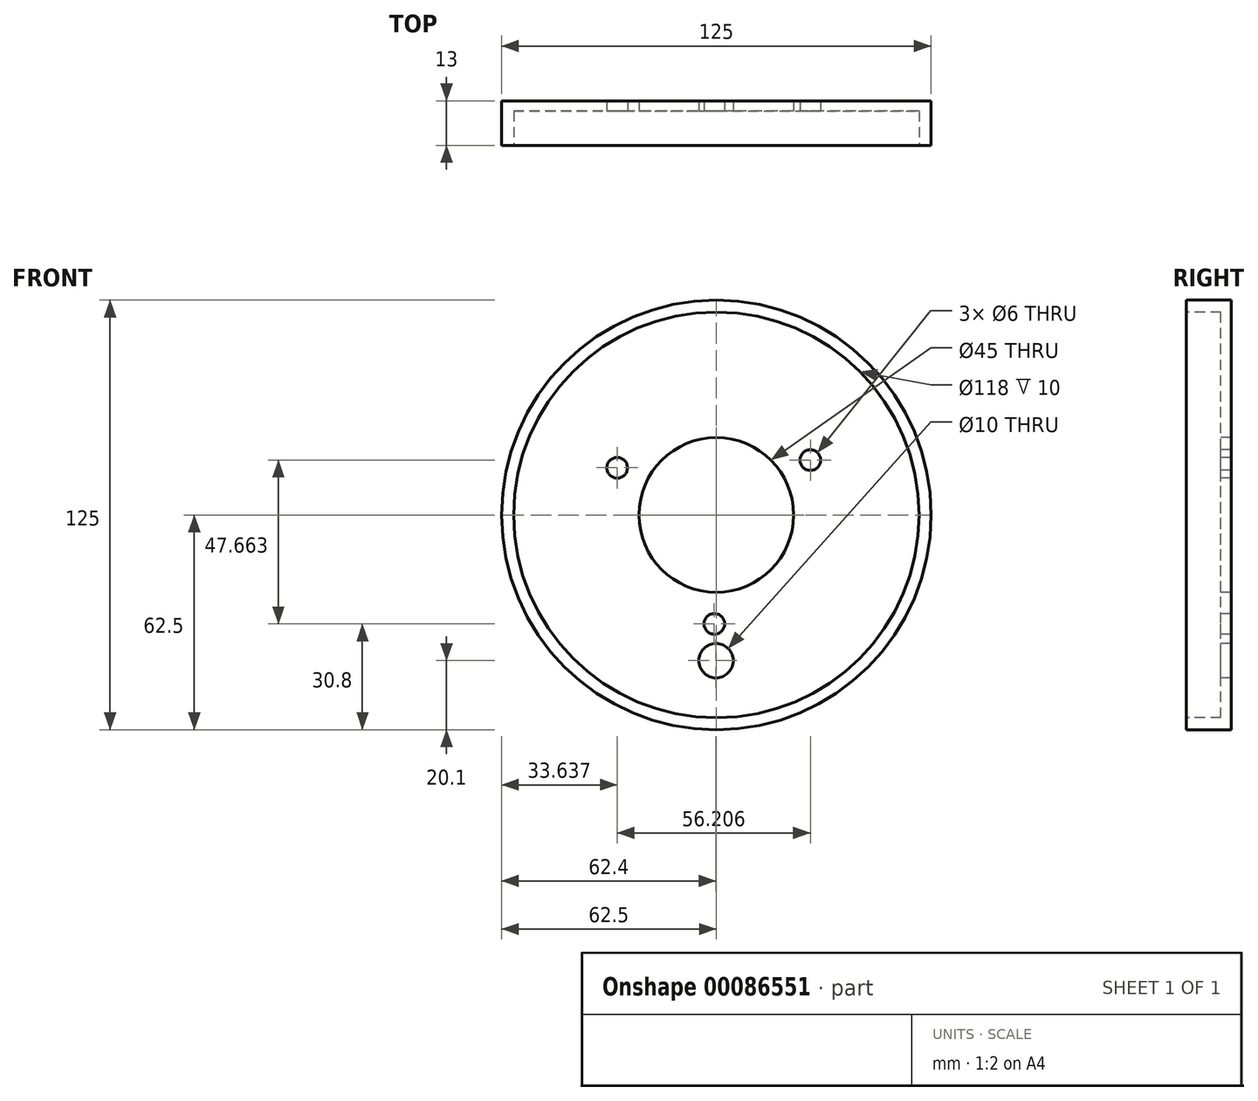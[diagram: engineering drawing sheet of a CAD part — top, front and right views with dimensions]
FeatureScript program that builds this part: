
annotation { "Feature Type Name" : "Feature", "Feature Type Description" : "" }
export const myFeature = defineFeature(function(context is Context, id is Id, definition is map)
    precondition{}
    {
        {
            var Q0;
            Q0=qCreatedBy(makeId("Front.planeOp"),FACE);
            var sketch = newSketch(context, id + "F0", { "sketchPlane" : qUnion([Q0])});
            skCircle(sketch, "E0", {"center": v(0, 0) * mm, "radius": 62.5 * mm});
            skSolve(sketch);
        }
        {
            var Q0;
            Q0=makeQuery(id+"F0.imprint","IMPRINT",FACE,{"disambiguationData":[TD([[makeQuery(id+"F0.imprint","IMPRINT",EDGE,{"derivedFrom":sQuery(id+"F0.wireOp",EDGE,"E0")}),1.0]])]});
            extrude(context, id + "F1", {"entities" : qUnion([Q0]), "offsetDistance" : 25 * mm, "depth" : 13 * mm});
        }
        {
            var Q0;
            Q0=makeQuery(id+"F1.opExtrude","CAP_FACE",FACE,{"disambiguationData":[OSD([sQuery(id+"F0.wireOp",EDGE,"E0")])],"isStart":false});
            var sketch = newSketch(context, id + "F2", { "sketchPlane" : qUnion([Q0])});
            skLineSegment(sketch, "E1.bottom", {"start": v(146.15, -111.65) * mm, "end": v(-146.15, -111.65) * mm});
            skLineSegment(sketch, "E1.top", {"start": v(146.15, 111.65) * mm, "end": v(-146.15, 111.65) * mm});
            skLineSegment(sketch, "E1.left", {"start": v(146.15, -111.65) * mm, "end": v(146.15, 111.65) * mm});
            skLineSegment(sketch, "E1.right", {"start": v(-146.15, -111.65) * mm, "end": v(-146.15, 111.65) * mm});
            skPoint(sketch, "E2", {"position": v(0, 0) * mm});
            skPoint(sketch, "E3", {"position": v(-28.86, 13.73) * mm});
            skPoint(sketch, "E4", {"position": v(27.34, 15.96) * mm});
            skPoint(sketch, "E5", {"position": v(-0.6, -31.7) * mm});
            skLineSegment(sketch, "E6", {"start": v(-28.86, 13.73) * mm, "end": v(27.34, 15.96) * mm, "construction": true});
            skPoint(sketch, "E7", {"position": v(-0.1, -42.4) * mm});
            skSolve(sketch);
        }
        {
            var Q0;
            Q0=sQuery(id+"F2.wireOp",VERTEX,"E3");
            var Q1;
            Q1=sQuery(id+"F2.wireOp",VERTEX,"E4");
            var Q2;
            Q2=sQuery(id+"F2.wireOp",VERTEX,"E5");
            var Q3;
            Q3=makeQuery(id+"F1.opExtrude","SWEPT_BODY",BODY,{"disambiguationData":[OSD([sQuery(id+"F0.wireOp",EDGE,"E0")])]});
            hole(context, id + "F3", {"style" : HoleStyle.SIMPLE, "endStyle" : HoleEndStyle.THROUGH, "holeDiameter" : 6 * mm, "majorDiameter" : 5 * mm, "locations" : qUnion([Q0, Q1, Q2]), "scope" : qUnion([Q3]), "isTappedThrough" : true, "tappedDepth" : 12 * mm, "tapClearance" : 3});
        }
        {
            var Q0;
            Q0=sQuery(id+"F2.wireOp",VERTEX,"E2");
            var Q1;
            Q1=makeQuery(id+"F1.opExtrude","SWEPT_BODY",BODY,{"disambiguationData":[OSD([sQuery(id+"F0.wireOp",EDGE,"E0")])]});
            hole(context, id + "F4", {"style" : HoleStyle.C_BORE, "endStyle" : HoleEndStyle.THROUGH, "holeDiameter" : 45 * mm, "cBoreDiameter" : 118 * mm, "cBoreDepth" : 10 * mm, "majorDiameter" : 5 * mm, "locations" : qUnion([Q0]), "scope" : qUnion([Q1]), "isTappedThrough" : true, "tappedDepth" : 12 * mm, "tapClearance" : 3});
        }
        {
            var Q0;
            Q0=sQuery(id+"F2.wireOp",VERTEX,"E7");
            var Q1;
            Q1=makeQuery(id+"F1.opExtrude","SWEPT_BODY",BODY,{"disambiguationData":[OSD([sQuery(id+"F0.wireOp",EDGE,"E0")])]});
            hole(context, id + "F5", {"style" : HoleStyle.SIMPLE, "endStyle" : HoleEndStyle.THROUGH, "holeDiameter" : 10 * mm, "majorDiameter" : 5 * mm, "locations" : qUnion([Q0]), "scope" : qUnion([Q1]), "isTappedThrough" : true, "tappedDepth" : 12 * mm, "tapClearance" : 3});
        }
    });
